# Revit family: Lollygagger Nisswa Sofa 96
name_source: partatom
category: Furniture
revit_build: Autodesk Revit 2016 (Build: 20150220_1215(x64)
units: mm (PartAtom-declared; Revit-internal decimal feet)

## family parameters
Always vertical = No
Cut with Voids When Loaded = No
OmniClass Number = 23.40.20.00
OmniClass Title = General Furniture and Specialties
Room Calculation Point = No
Shared = No
Work Plane-Based = No

## types (10) — shared parameters
Height = 28 1/8"
Length = 94 1/2"
Manufacturer = Loll
Radio = 1"
Thick = 1/2"
Type Image = Nisswa Sofa 96.jpg
URL = https://lolldesigns.com
Width = 31 19/32"

## per-type parameters (varying)
| type | Finish Material | Sunbrella Back2 |
| Loll-Black | Loll-White | Jockey Red - Loll Design |
| Loll-Sunset | Loll-Sunset | Jockey Red - Loll Design |
| Loll-Chocolate | Loll-Chocolate | Jockey Red - Loll Design |
| Loll-Sky | Loll-Sky | White Canvas - Loll Design |
| Loll-Apple | Loll-Apple | Jockey Red - Loll Design |
| Loll-Leaf | Loll-Leaf | Jockey Red - Loll Design |
| Loll-Charcoal | Loll-Charcoal | Jockey Red - Loll Design |
| Loll-Navy Blue | Loll-Navy Blue | Jockey Red - Loll Design |
| Loll-White | Loll-White | Jockey Red - Loll Design |
| Loll-Driftwood | Loll-Driftwood | Jockey Red - Loll Design |

## geometry (parser evidence)
native form markers: Blend x2, Sweep x3
no freeform markers — native parametric forms only
